# Revit family: ASSA_ABLOY_VersaMax_OHC_FBO02
name_source: partatom
category: Doors
units: mm (PartAtom-declared; Revit-internal decimal feet)

## family parameters
Always vertical = Yes
Cut with Voids When Loaded = No
Host = Wall
OmniClass Number = 23.30.10.00
OmniClass Title = Doors
Room Calculation Point = No
Shared = No

## types (4) — shared parameters
Analytic Construction = <None>
BIMobject category = Sliding Doors
Bottom Profile Height = Versamax Slide Leaf S Rated : 0' 4''
Bottom Profile Option 01 = Versamax Slide Leaf S Rated : 0' 4''
Bottom Profile Option 02 = Versamax Slide Leaf S Rated : 0' 7''
Bottom Profile Option 03 = Versamax Slide Leaf S Rated : 0' 10''
Brass Polished Finish = Brass, Polished
Brass Satin Finish = Brass, Satin
Clear Anodized = Clear Anodized
Dark Bronze Anodized = Dark Bronze Anodized
Date of publishing = 2015-02-23
Depth = 0.00
Edition number = 1
Frame Material = Clear Anodized
Gap = 6 mm  [stored 0.019685 ft]
Glass = Glass
Header = 127 mm  [stored 0.416667 ft]
Height = 2280 mm
IFC Classification = Door
Manufacturer = ASSA ABLOY Entrance Systems-North America
Manufacturer name = ASSA ABLOY Entrance Systems-North America
Material main = Aluminium
NBS Reference Code = 25-30-20-77
NBS Reference Description = Sliding Doorset Systems
Nominal height = 0.00
Nominal width = 0.00
Product SKU = VersaMax_OHC
Product data url = http://besam-na.bimobject.com
Product family = ICU
Product group = Overhead Concealed
QR code = http://besam-na.bimobject.com
Rough Height = 2286 mm  [stored 7.5 ft]
Rubber = Rubber, Black
Stainless Steel Polished Finish = Stainless Steel, Polished
Stainless Steel Satin Finish = Stainless Steel, Satin
UNSPSC Code = 301715
Uniclass 1.4 Code = L4133
Uniclass 1.4 Description = Sliding
Uniclass 2.0 Code = SS-25-30-20-77
Uniclass 2.0 Description = Sliding Doorset Systems
Wall Closure = By host
Weight Net (Kg) = 0
zero-valued in all types: Thickness

## per-type parameters (varying)
| type | Rough Width | Width |
| ICU-SE-FBO-7 | 2146 mm | 2134 mm |
| ICU-SE-FBO-8 | 2451 mm | 2438 mm |
| ICU-SE-FBO-8-6 | 2604 mm | 2591 mm |
| ICU-SE-FBO-9 | 2756 mm | 2743 mm |

note: [stored X ft] marks values corroborated as IEEE doubles in the binary element streams (Revit-internal decimal feet)

## geometry (parser evidence)
native form markers: Sweep x24
no freeform markers — native parametric forms only
